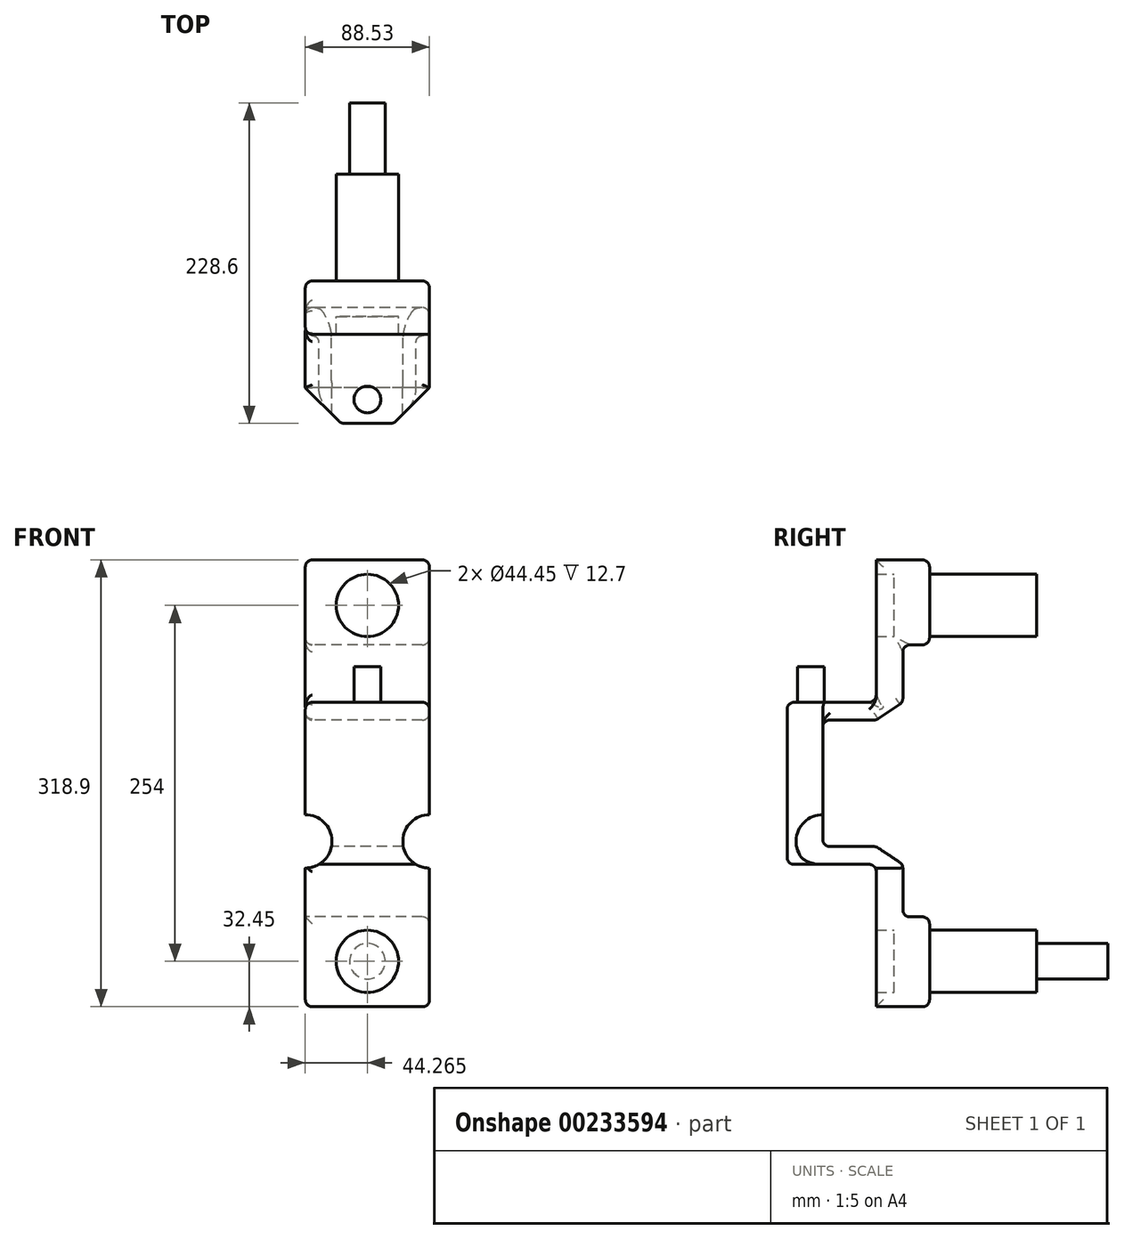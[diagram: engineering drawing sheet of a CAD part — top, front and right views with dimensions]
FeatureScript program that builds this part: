
annotation { "Feature Type Name" : "Feature", "Feature Type Description" : "" }
export const myFeature = defineFeature(function(context is Context, id is Id, definition is map)
    precondition{}
    {
        {
            var Q0;
            Q0=qCreatedBy(makeId("Front.planeOp"),FACE);
            var sketch = newSketch(context, id + "F0", { "sketchPlane" : qUnion([Q0])});
            skPoint(sketch, "E0.middle", {"position": v(-200.62, 122.45) * mm});
            skCircle(sketch, "E1", {"center": v(-200.62, 122.45) * mm, "radius": 22.23 * mm});
            skCircle(sketch, "E2", {"center": v(-200.62, -131.55) * mm, "radius": 22.23 * mm});
            skLineSegment(sketch, "E3", {"start": v(-200.62, 122.45) * mm, "end": v(-200.62, -131.55) * mm, "construction": true});
            skLineSegment(sketch, "E4.bottom", {"start": v(-156.36, -164) * mm, "end": v(-244.9, -164) * mm});
            skLineSegment(sketch, "E4.top", {"start": v(-156.36, 154.9) * mm, "end": v(-244.9, 154.9) * mm});
            skLineSegment(sketch, "E4.left", {"start": v(-156.36, -164) * mm, "end": v(-156.36, 154.9) * mm});
            skLineSegment(sketch, "E4.right", {"start": v(-244.9, -164) * mm, "end": v(-244.9, 154.9) * mm});
            skPoint(sketch, "E4.middle", {"position": v(-200.62, -4.55) * mm});
            skSolve(sketch);
        }
        {
            var Q0;
            Q0=qSketchRegion(id+"F0",true);
            extrude(context, id + "F1", {"entities" : qUnion([Q0]), "depth" : 76.2 * mm});
        }
        {
            var Q0;
            Q0=makeQuery(id+"F1.opExtrude","SWEPT_FACE",FACE,{"disambiguationData":[OSD([sQuery(id+"F0.wireOp",EDGE,"E4.right")])]});
            var sketch = newSketch(context, id + "F2", { "sketchPlane" : qUnion([Q0])});
            skLineSegment(sketch, "E5", {"start": v(76.2, 154.9) * mm, "end": v(76.2, 53.3) * mm, "construction": true});
            skLineSegment(sketch, "E6", {"start": v(76.2, -164) * mm, "end": v(50.8, -164) * mm, "construction": true});
            skLineSegment(sketch, "E7", {"start": v(76.2, -164) * mm, "end": v(76.2, -62.4) * mm, "construction": true});
            skLineSegment(sketch, "E8", {"start": v(76.2, 154.9) * mm, "end": v(50.8, 154.9) * mm, "construction": true});
            skLineSegment(sketch, "E9", {"start": v(38.1, 154.9) * mm, "end": v(76.2, 53.3) * mm});
            skLineSegment(sketch, "E10", {"start": v(76.2, -62.4) * mm, "end": v(38.1, -164) * mm});
            skSolve(sketch);
        }
        {
            var Q0;
            {var subQ0=sQuery(id+"F2.wireOp",EDGE,"E10");Q0=makeQuery(id+"F2.imprint","IMPRINT",FACE,{"disambiguationData":[TD([[makeQuery(id+"F2.imprint","IMPRINT",EDGE,{"derivedFrom":subQ0}),1.0]])]});}
            var Q1;
            {var subQ0=sQuery(id+"F2.wireOp",EDGE,"E9");Q1=makeQuery(id+"F2.imprint","IMPRINT",FACE,{"disambiguationData":[TD([[makeQuery(id+"F2.imprint","IMPRINT",EDGE,{"derivedFrom":subQ0}),1.0]])]});}
            extrude(context, id + "F3", {"entities" : qUnion([Q0, Q1]), "operationType" : NewBodyOperationType.REMOVE, "endBound" : BoundingType.THROUGH_ALL, "oppositeDirection" : true, "depth" : 25.4 * mm});
        }
        {
            var Q0;
            Q0=makeQuery(id+"F0.imprint","IMPRINT",FACE,{"disambiguationData":[TD([[makeQuery(id+"F0.imprint","IMPRINT",EDGE,{"derivedFrom":sQuery(id+"F0.wireOp",EDGE,"E1")}),1.0]])]});
            var Q1;
            Q1=makeQuery(id+"F0.imprint","IMPRINT",FACE,{"disambiguationData":[TD([[makeQuery(id+"F0.imprint","IMPRINT",EDGE,{"derivedFrom":sQuery(id+"F0.wireOp",EDGE,"E2")}),1.0]])]});
            extrude(context, id + "F4", {"entities" : qUnion([Q0, Q1]), "operationType" : NewBodyOperationType.ADD, "depth" : 25.4 * mm, "hasSecondDirection" : true, "secondDirectionOppositeDirection" : true, "secondDirectionDepth" : 76.2 * mm});
        }
        {
            var Q0;
            Q0=makeQuery(id+"F1.opExtrude","SWEPT_FACE",FACE,{"disambiguationData":[OSD([sQuery(id+"F0.wireOp",EDGE,"E4.left")])]});
            var sketch = newSketch(context, id + "F5", { "sketchPlane" : qUnion([Q0])});
            skLineSegment(sketch, "E11", {"start": v(-38.1, 154.9) * mm, "end": v(-38.1, 53.3) * mm});
            skLineSegment(sketch, "E12", {"start": v(-38.1, 53.3) * mm, "end": v(-76.2, 53.3) * mm});
            skLineSegment(sketch, "E13", {"start": v(-76.2, -62.4) * mm, "end": v(-38.1, -62.4) * mm});
            skLineSegment(sketch, "E14", {"start": v(-38.1, -62.4) * mm, "end": v(-38.1, -164) * mm});
            skSolve(sketch);
        }
        {
            var Q0;
            Q0=makeQuery(id+"F5.imprint","IMPRINT",FACE,{"disambiguationData":[TD([[makeQuery(id+"F5.imprint","IMPRINT",EDGE,{"derivedFrom":sQuery(id+"F5.wireOp",EDGE,"E13")}),-1.0]])]});
            var Q1;
            Q1=makeQuery(id+"F5.imprint","IMPRINT",FACE,{"disambiguationData":[TD([[makeQuery(id+"F5.imprint","IMPRINT",EDGE,{"derivedFrom":sQuery(id+"F5.wireOp",EDGE,"E11")}),-1.0]])]});
            extrude(context, id + "F6", {"entities" : qUnion([Q0, Q1]), "operationType" : NewBodyOperationType.REMOVE, "endBound" : BoundingType.THROUGH_ALL, "oppositeDirection" : true, "depth" : 25.4 * mm});
        }
        {
            var Q0;
            Q0=makeQuery(id+"F4.opExtrude","CAP_FACE",FACE,{"disambiguationData":[OSD([sQuery(id+"F0.wireOp",EDGE,"E2")])],"isStart":true});
            extrude(context, id + "F7", {"entities" : qUnion([Q0]), "operationType" : NewBodyOperationType.ADD, "depth" : 50.8 * mm});
        }
        {
            var Q0;
            Q0=makeQuery(id+"F7.opExtrude","CAP_FACE",FACE,{"disambiguationData":[OSD([sQuery(id+"F0.wireOp",EDGE,"E2")])],"isStart":false});
            var sketch = newSketch(context, id + "F8", { "sketchPlane" : qUnion([Q0])});
            skCircle(sketch, "E15", {"center": v(200.62, -131.55) * mm, "radius": 12.7 * mm});
            skSolve(sketch);
        }
        {
            var Q0;
            Q0=makeQuery(id+"F8.imprint","IMPRINT",FACE,{"disambiguationData":[TD([[makeQuery(id+"F8.imprint","IMPRINT",EDGE,{"derivedFrom":sQuery(id+"F8.wireOp",EDGE,"E15")}),-1.0]])]});
            extrude(context, id + "F9", {"entities" : qUnion([Q0]), "operationType" : NewBodyOperationType.REMOVE, "oppositeDirection" : true, "depth" : 50.8 * mm});
        }
        {
            var Q0;
            Q0=makeQuery(id+"F1.opExtrude","CAP_FACE",FACE,{"disambiguationData":[OSD([sQuery(id+"F0.wireOp",EDGE,"E1"),sQuery(id+"F0.wireOp",EDGE,"E2"),sQuery(id+"F0.wireOp",EDGE,"E4.bottom"),sQuery(id+"F0.wireOp",EDGE,"E4.top"),sQuery(id+"F0.wireOp",EDGE,"E4.left"),sQuery(id+"F0.wireOp",EDGE,"E4.right")])],"isStart":false});
            extrude(context, id + "F10", {"entities" : qUnion([Q0]), "operationType" : NewBodyOperationType.ADD, "depth" : 25.4 * mm});
        }
        {
            var Q0;
            {var subQ0=sQuery(id+"F5.wireOp",EDGE,"E12");Q0=makeQuery(id+"F10.boolean.opBoolean","MERGE",FACE,{"derivedFrom":[makeQuery(id+"F6.boolean.opBoolean","COPY",FACE,{"derivedFrom":makeQuery(id+"F6.opExtrude","SWEPT_FACE",FACE,{"disambiguationData":[OSD([subQ0])]})}),makeQuery(id+"F10.opExtrude","SWEPT_FACE",FACE,{"disambiguationData":[OSD([sQuery(id+"F0.wireOp",EDGE,"E4.left"),sQuery(id+"F0.wireOp",EDGE,"E4.right"),sQuery(id+"F2.wireOp",EDGE,"E9"),subQ0])]})]});}
            var sketch = newSketch(context, id + "F11", { "sketchPlane" : qUnion([Q0])});
            skCircle(sketch, "E16", {"center": v(-200.62, -84.67) * mm, "radius": 9.53 * mm});
            skPoint(sketch, "E16.centerSnap0", {"position": v(-200.62, -101.6) * mm});
            skSolve(sketch);
        }
        {
            var Q0;
            Q0=makeQuery(id+"F11.imprint","IMPRINT",FACE,{"disambiguationData":[TD([[makeQuery(id+"F11.imprint","IMPRINT",EDGE,{"derivedFrom":sQuery(id+"F11.wireOp",EDGE,"E16")}),1.0]])]});
            extrude(context, id + "F12", {"entities" : qUnion([Q0]), "operationType" : NewBodyOperationType.ADD, "depth" : 25.4 * mm});
        }
        {
            var Q0;
            Q0=makeQuery(id+"F10.opExtrude","CAP_EDGE",EDGE,{"disambiguationData":[OSD([sQuery(id+"F0.wireOp",EDGE,"E4.right")])],"isStart":false});
            var Q1;
            Q1=makeQuery(id+"F10.opExtrude","CAP_EDGE",EDGE,{"disambiguationData":[OSD([sQuery(id+"F0.wireOp",EDGE,"E4.left")])],"isStart":false});
            chamfer(context, id + "F13", {"entities" : qUnion([Q0, Q1]), "width" : 25.4 * mm, "tangentPropagation" : true});
        }
        {
            var Q0;
            {var subQ0=sQuery(id+"F0.wireOp",EDGE,"E4.right");Q0=makeQuery(id+"F10.boolean.opBoolean","MERGE",FACE,{"derivedFrom":[makeQuery(id+"F1.opExtrude","SWEPT_FACE",FACE,{"disambiguationData":[OSD([subQ0])]}),makeQuery(id+"F10.opExtrude","SWEPT_FACE",FACE,{"disambiguationData":[OSD([subQ0])]})]});}
            var sketch = newSketch(context, id + "F14", { "sketchPlane" : qUnion([Q0])});
            skLineSegment(sketch, "E17", {"start": v(0, 94.28) * mm, "end": v(19.05, 94.28) * mm});
            skLineSegment(sketch, "E18", {"start": v(19.05, 94.28) * mm, "end": v(19.05, 53.3) * mm});
            skLineSegment(sketch, "E19", {"start": v(19.05, -99.86) * mm, "end": v(0, -99.86) * mm});
            skLineSegment(sketch, "E20.0", {"start": v(76.2, 40.6) * mm, "end": v(38.1, 40.6) * mm});
            skLineSegment(sketch, "E21.0", {"start": v(38.1, -49.7) * mm, "end": v(76.2, -49.7) * mm});
            skLineSegment(sketch, "E22", {"start": v(38.1, 40.6) * mm, "end": v(19.05, 53.3) * mm});
            skLineSegment(sketch, "E23", {"start": v(38.1, -49.7) * mm, "end": v(19.05, -62.4) * mm});
            skLineSegment(sketch, "E24.trimOffspring", {"start": v(19.05, -62.4) * mm, "end": v(19.05, -99.86) * mm});
            skSolve(sketch);
        }
        {
            var Q0;
            {var subQ2=sQuery(id+"F14.wireOp",EDGE,"E17");Q0=makeQuery(id+"F14.imprint","IMPRINT",FACE,{"disambiguationData":[TD([[makeQuery(id+"F14.imprint","IMPRINT",EDGE,{"derivedFrom":subQ2}),-1.0]])]});}
            extrude(context, id + "F15", {"entities" : qUnion([Q0]), "operationType" : NewBodyOperationType.REMOVE, "endBound" : BoundingType.THROUGH_ALL, "oppositeDirection" : true, "depth" : 25.4 * mm});
        }
        {
            var Q0;
            {var subQ0=sQuery(id+"F5.wireOp",EDGE,"E13");var subQ1=sQuery(id+"F0.wireOp",EDGE,"E4.left");Q0=makeQuery(id+"F13.opChamfer","BLEND_EDGE",EDGE,{"blendedFrom":[makeQuery(id+"F10.opExtrude","CAP_EDGE",EDGE,{"disambiguationData":[OSD([subQ1])],"isStart":false}),makeQuery(id+"F10.boolean.opBoolean","MERGE",FACE,{"derivedFrom":[makeQuery(id+"F6.boolean.opBoolean","COPY",FACE,{"derivedFrom":makeQuery(id+"F6.opExtrude","SWEPT_FACE",FACE,{"disambiguationData":[OSD([subQ0])]})}),makeQuery(id+"F10.opExtrude","SWEPT_FACE",FACE,{"disambiguationData":[OSD([subQ1,sQuery(id+"F0.wireOp",EDGE,"E4.right"),sQuery(id+"F2.wireOp",EDGE,"E10"),subQ0])]})]})],"blendedInto":[makeQuery(id+"F10.boolean.opBoolean","MERGE",FACE,{"derivedFrom":[makeQuery(id+"F6.boolean.opBoolean","COPY",FACE,{"derivedFrom":makeQuery(id+"F6.opExtrude","SWEPT_FACE",FACE,{"disambiguationData":[OSD([subQ0])]})}),makeQuery(id+"F10.opExtrude","SWEPT_FACE",FACE,{"disambiguationData":[OSD([subQ1,sQuery(id+"F0.wireOp",EDGE,"E4.right"),sQuery(id+"F2.wireOp",EDGE,"E10"),subQ0])]})]})]});}
            var Q1;
            Q1=makeQuery(id+"F10.opExtrude","CAP_EDGE",EDGE,{"disambiguationData":[OSD([sQuery(id+"F0.wireOp",EDGE,"E4.left"),sQuery(id+"F0.wireOp",EDGE,"E4.right"),sQuery(id+"F2.wireOp",EDGE,"E10"),sQuery(id+"F5.wireOp",EDGE,"E13")])],"isStart":false});
            var Q2;
            {var subQ0=sQuery(id+"F5.wireOp",EDGE,"E13");var subQ1=sQuery(id+"F0.wireOp",EDGE,"E4.right");Q2=makeQuery(id+"F13.opChamfer","BLEND_EDGE",EDGE,{"blendedFrom":[makeQuery(id+"F10.opExtrude","CAP_EDGE",EDGE,{"disambiguationData":[OSD([subQ1])],"isStart":false}),makeQuery(id+"F10.boolean.opBoolean","MERGE",FACE,{"derivedFrom":[makeQuery(id+"F6.boolean.opBoolean","COPY",FACE,{"derivedFrom":makeQuery(id+"F6.opExtrude","SWEPT_FACE",FACE,{"disambiguationData":[OSD([subQ0])]})}),makeQuery(id+"F10.opExtrude","SWEPT_FACE",FACE,{"disambiguationData":[OSD([sQuery(id+"F0.wireOp",EDGE,"E4.left"),subQ1,sQuery(id+"F2.wireOp",EDGE,"E10"),subQ0])]})]})],"blendedInto":[makeQuery(id+"F10.boolean.opBoolean","MERGE",FACE,{"derivedFrom":[makeQuery(id+"F6.boolean.opBoolean","COPY",FACE,{"derivedFrom":makeQuery(id+"F6.opExtrude","SWEPT_FACE",FACE,{"disambiguationData":[OSD([subQ0])]})}),makeQuery(id+"F10.opExtrude","SWEPT_FACE",FACE,{"disambiguationData":[OSD([sQuery(id+"F0.wireOp",EDGE,"E4.left"),subQ1,sQuery(id+"F2.wireOp",EDGE,"E10"),subQ0])]})]})]});}
            var Q3;
            {var subQ0=sQuery(id+"F0.wireOp",EDGE,"E4.right");Q3=makeQuery(id+"F10.boolean.opBoolean","MERGE",EDGE,{"derivedFrom":[makeQuery(id+"F6.boolean.opBoolean","INTERSECT",EDGE,{"derivedFrom":[makeQuery(id+"F1.opExtrude","SWEPT_FACE",FACE,{"disambiguationData":[OSD([subQ0])]}),makeQuery(id+"F6.opExtrude","SWEPT_FACE",FACE,{"disambiguationData":[OSD([sQuery(id+"F5.wireOp",EDGE,"E13")])]})]}),makeQuery(id+"F10.opExtrude","SWEPT_EDGE",EDGE,{"disambiguationData":[OSD([subQ0,sQuery(id+"F2.wireOp",EDGE,"E10")])]})]});}
            var Q4;
            Q4=makeQuery(id+"F6.boolean.opBoolean","INTERSECT",EDGE,{"derivedFrom":[makeQuery(id+"F1.opExtrude","SWEPT_FACE",FACE,{"disambiguationData":[OSD([sQuery(id+"F0.wireOp",EDGE,"E4.right")])]}),makeQuery(id+"F6.opExtrude","SWEPT_FACE",FACE,{"disambiguationData":[OSD([sQuery(id+"F5.wireOp",EDGE,"E14")])]})]});
            var Q5;
            {var subQ0=sQuery(id+"F2.wireOp",EDGE,"E10");var subQ1=sQuery(id+"F0.wireOp",EDGE,"E4.bottom");Q5=makeQuery(id+"F6.boolean.opBoolean","MERGE",EDGE,{"derivedFrom":[makeQuery(id+"F3.boolean.opBoolean","COPY",EDGE,{"derivedFrom":makeQuery(id+"F3.opExtrude","SWEPT_EDGE",EDGE,{"disambiguationData":[OSD([subQ1,sQuery(id+"F0.wireOp",EDGE,"E4.right"),subQ0])]})}),makeQuery(id+"F6.opExtrude","SWEPT_EDGE",EDGE,{"disambiguationData":[OSD([subQ1,sQuery(id+"F0.wireOp",EDGE,"E4.left"),subQ0,sQuery(id+"F5.wireOp",EDGE,"E14")])]})]});}
            var Q6;
            Q6=makeQuery(id+"F6.boolean.opBoolean","COPY",EDGE,{"derivedFrom":makeQuery(id+"F6.opExtrude","CAP_EDGE",EDGE,{"disambiguationData":[OSD([sQuery(id+"F5.wireOp",EDGE,"E14")])],"isStart":true})});
            var Q7;
            {var subQ0=sQuery(id+"F5.wireOp",EDGE,"E13");Q7=makeQuery(id+"F10.boolean.opBoolean","MERGE",EDGE,{"derivedFrom":[makeQuery(id+"F6.boolean.opBoolean","COPY",EDGE,{"derivedFrom":makeQuery(id+"F6.opExtrude","CAP_EDGE",EDGE,{"disambiguationData":[OSD([subQ0])],"isStart":true})}),makeQuery(id+"F10.opExtrude","SWEPT_EDGE",EDGE,{"disambiguationData":[OSD([sQuery(id+"F0.wireOp",EDGE,"E4.left"),sQuery(id+"F2.wireOp",EDGE,"E10"),subQ0])]})]});}
            var Q8;
            {var subQ0=sQuery(id+"F0.wireOp",EDGE,"E4.left");Q8=makeQuery(id+"F13.opChamfer","BLEND_EDGE",EDGE,{"blendedFrom":[makeQuery(id+"F10.opExtrude","CAP_EDGE",EDGE,{"disambiguationData":[OSD([subQ0])],"isStart":false}),makeQuery(id+"F10.opExtrude","CAP_FACE",FACE,{"disambiguationData":[OSD([sQuery(id+"F0.wireOp",EDGE,"E1"),sQuery(id+"F0.wireOp",EDGE,"E2"),sQuery(id+"F0.wireOp",EDGE,"E4.bottom"),sQuery(id+"F0.wireOp",EDGE,"E4.top"),subQ0,sQuery(id+"F0.wireOp",EDGE,"E4.right")])],"isStart":false})],"blendedInto":[makeQuery(id+"F10.opExtrude","CAP_FACE",FACE,{"disambiguationData":[OSD([sQuery(id+"F0.wireOp",EDGE,"E1"),sQuery(id+"F0.wireOp",EDGE,"E2"),sQuery(id+"F0.wireOp",EDGE,"E4.bottom"),sQuery(id+"F0.wireOp",EDGE,"E4.top"),subQ0,sQuery(id+"F0.wireOp",EDGE,"E4.right")])],"isStart":false})]});}
            var Q9;
            {var subQ0=sQuery(id+"F0.wireOp",EDGE,"E4.right");Q9=makeQuery(id+"F13.opChamfer","BLEND_EDGE",EDGE,{"blendedFrom":[makeQuery(id+"F10.opExtrude","CAP_EDGE",EDGE,{"disambiguationData":[OSD([subQ0])],"isStart":false}),makeQuery(id+"F10.opExtrude","CAP_FACE",FACE,{"disambiguationData":[OSD([sQuery(id+"F0.wireOp",EDGE,"E1"),sQuery(id+"F0.wireOp",EDGE,"E2"),sQuery(id+"F0.wireOp",EDGE,"E4.bottom"),sQuery(id+"F0.wireOp",EDGE,"E4.top"),sQuery(id+"F0.wireOp",EDGE,"E4.left"),subQ0])],"isStart":false})],"blendedInto":[makeQuery(id+"F10.opExtrude","CAP_FACE",FACE,{"disambiguationData":[OSD([sQuery(id+"F0.wireOp",EDGE,"E1"),sQuery(id+"F0.wireOp",EDGE,"E2"),sQuery(id+"F0.wireOp",EDGE,"E4.bottom"),sQuery(id+"F0.wireOp",EDGE,"E4.top"),sQuery(id+"F0.wireOp",EDGE,"E4.left"),subQ0])],"isStart":false})]});}
            var Q10;
            {var subQ0=sQuery(id+"F5.wireOp",EDGE,"E12");var subQ1=sQuery(id+"F0.wireOp",EDGE,"E4.left");Q10=makeQuery(id+"F13.opChamfer","BLEND_EDGE",EDGE,{"blendedFrom":[makeQuery(id+"F10.opExtrude","CAP_EDGE",EDGE,{"disambiguationData":[OSD([subQ1])],"isStart":false}),makeQuery(id+"F10.boolean.opBoolean","MERGE",FACE,{"derivedFrom":[makeQuery(id+"F6.boolean.opBoolean","COPY",FACE,{"derivedFrom":makeQuery(id+"F6.opExtrude","SWEPT_FACE",FACE,{"disambiguationData":[OSD([subQ0])]})}),makeQuery(id+"F10.opExtrude","SWEPT_FACE",FACE,{"disambiguationData":[OSD([subQ1,sQuery(id+"F0.wireOp",EDGE,"E4.right"),sQuery(id+"F2.wireOp",EDGE,"E9"),subQ0])]})]})],"blendedInto":[makeQuery(id+"F10.boolean.opBoolean","MERGE",FACE,{"derivedFrom":[makeQuery(id+"F6.boolean.opBoolean","COPY",FACE,{"derivedFrom":makeQuery(id+"F6.opExtrude","SWEPT_FACE",FACE,{"disambiguationData":[OSD([subQ0])]})}),makeQuery(id+"F10.opExtrude","SWEPT_FACE",FACE,{"disambiguationData":[OSD([subQ1,sQuery(id+"F0.wireOp",EDGE,"E4.right"),sQuery(id+"F2.wireOp",EDGE,"E9"),subQ0])]})]})]});}
            var Q11;
            Q11=makeQuery(id+"F10.opExtrude","CAP_EDGE",EDGE,{"disambiguationData":[OSD([sQuery(id+"F0.wireOp",EDGE,"E4.left"),sQuery(id+"F0.wireOp",EDGE,"E4.right"),sQuery(id+"F2.wireOp",EDGE,"E9"),sQuery(id+"F5.wireOp",EDGE,"E12")])],"isStart":false});
            var Q12;
            {var subQ0=sQuery(id+"F5.wireOp",EDGE,"E12");var subQ1=sQuery(id+"F0.wireOp",EDGE,"E4.right");Q12=makeQuery(id+"F13.opChamfer","BLEND_EDGE",EDGE,{"blendedFrom":[makeQuery(id+"F10.opExtrude","CAP_EDGE",EDGE,{"disambiguationData":[OSD([subQ1])],"isStart":false}),makeQuery(id+"F10.boolean.opBoolean","MERGE",FACE,{"derivedFrom":[makeQuery(id+"F6.boolean.opBoolean","COPY",FACE,{"derivedFrom":makeQuery(id+"F6.opExtrude","SWEPT_FACE",FACE,{"disambiguationData":[OSD([subQ0])]})}),makeQuery(id+"F10.opExtrude","SWEPT_FACE",FACE,{"disambiguationData":[OSD([sQuery(id+"F0.wireOp",EDGE,"E4.left"),subQ1,sQuery(id+"F2.wireOp",EDGE,"E9"),subQ0])]})]})],"blendedInto":[makeQuery(id+"F10.boolean.opBoolean","MERGE",FACE,{"derivedFrom":[makeQuery(id+"F6.boolean.opBoolean","COPY",FACE,{"derivedFrom":makeQuery(id+"F6.opExtrude","SWEPT_FACE",FACE,{"disambiguationData":[OSD([subQ0])]})}),makeQuery(id+"F10.opExtrude","SWEPT_FACE",FACE,{"disambiguationData":[OSD([sQuery(id+"F0.wireOp",EDGE,"E4.left"),subQ1,sQuery(id+"F2.wireOp",EDGE,"E9"),subQ0])]})]})]});}
            var Q13;
            Q13=makeQuery(id+"F6.boolean.opBoolean","INTERSECT",EDGE,{"derivedFrom":[makeQuery(id+"F1.opExtrude","SWEPT_FACE",FACE,{"disambiguationData":[OSD([sQuery(id+"F0.wireOp",EDGE,"E4.right")])]}),makeQuery(id+"F6.opExtrude","SWEPT_FACE",FACE,{"disambiguationData":[OSD([sQuery(id+"F5.wireOp",EDGE,"E11")])]})]});
            var Q14;
            {var subQ0=sQuery(id+"F2.wireOp",EDGE,"E9");var subQ1=sQuery(id+"F0.wireOp",EDGE,"E4.top");Q14=makeQuery(id+"F6.boolean.opBoolean","MERGE",EDGE,{"derivedFrom":[makeQuery(id+"F3.boolean.opBoolean","COPY",EDGE,{"derivedFrom":makeQuery(id+"F3.opExtrude","SWEPT_EDGE",EDGE,{"disambiguationData":[OSD([subQ1,sQuery(id+"F0.wireOp",EDGE,"E4.right"),subQ0])]})}),makeQuery(id+"F6.opExtrude","SWEPT_EDGE",EDGE,{"disambiguationData":[OSD([subQ1,sQuery(id+"F0.wireOp",EDGE,"E4.left"),subQ0,sQuery(id+"F5.wireOp",EDGE,"E11")])]})]});}
            var Q15;
            Q15=makeQuery(id+"F6.boolean.opBoolean","COPY",EDGE,{"derivedFrom":makeQuery(id+"F6.opExtrude","CAP_EDGE",EDGE,{"disambiguationData":[OSD([sQuery(id+"F5.wireOp",EDGE,"E11")])],"isStart":true})});
            var Q16;
            Q16=makeQuery(id+"F1.opExtrude","SWEPT_EDGE",EDGE,{"disambiguationData":[OSD([sQuery(id+"F0.wireOp",EDGE,"E4.top"),sQuery(id+"F0.wireOp",EDGE,"E4.left")])]});
            var Q17;
            {var subQ0=sQuery(id+"F0.wireOp",EDGE,"E4.left");var subQ1=sQuery(id+"F0.wireOp",EDGE,"E4.top");Q17=makeQuery(id+"F15.boolean.opBoolean","SPLIT",EDGE,{"disambiguationData":[TD([makeQuery(id+"F1.opExtrude","SWEPT_FACE",FACE,{"disambiguationData":[OSD([subQ1])]})])],"derivedFrom":makeQuery(id+"F1.opExtrude","CAP_EDGE",EDGE,{"disambiguationData":[OSD([subQ0])],"isStart":true})});}
            var Q18;
            {var subQ0=sQuery(id+"F0.wireOp",EDGE,"E4.left");Q18=makeQuery(id+"F15.boolean.opBoolean","INTERSECT",EDGE,{"derivedFrom":[makeQuery(id+"F10.boolean.opBoolean","MERGE",FACE,{"derivedFrom":[makeQuery(id+"F1.opExtrude","SWEPT_FACE",FACE,{"disambiguationData":[OSD([subQ0])]}),makeQuery(id+"F10.opExtrude","SWEPT_FACE",FACE,{"disambiguationData":[OSD([subQ0])]})]}),makeQuery(id+"F15.opExtrude","SWEPT_FACE",FACE,{"disambiguationData":[OSD([sQuery(id+"F14.wireOp",EDGE,"E21.0")])]})]});}
            var Q19;
            {var subQ0=sQuery(id+"F0.wireOp",EDGE,"E4.left");Q19=makeQuery(id+"F15.boolean.opBoolean","INTERSECT",EDGE,{"derivedFrom":[makeQuery(id+"F10.boolean.opBoolean","MERGE",FACE,{"derivedFrom":[makeQuery(id+"F1.opExtrude","SWEPT_FACE",FACE,{"disambiguationData":[OSD([subQ0])]}),makeQuery(id+"F10.opExtrude","SWEPT_FACE",FACE,{"disambiguationData":[OSD([subQ0])]})]}),makeQuery(id+"F15.opExtrude","SWEPT_FACE",FACE,{"disambiguationData":[OSD([sQuery(id+"F14.wireOp",EDGE,"E23")])]})]});}
            var Q20;
            {var subQ0=sQuery(id+"F0.wireOp",EDGE,"E4.left");Q20=makeQuery(id+"F15.boolean.opBoolean","INTERSECT",EDGE,{"derivedFrom":[makeQuery(id+"F10.boolean.opBoolean","MERGE",FACE,{"derivedFrom":[makeQuery(id+"F1.opExtrude","SWEPT_FACE",FACE,{"disambiguationData":[OSD([subQ0])]}),makeQuery(id+"F10.opExtrude","SWEPT_FACE",FACE,{"disambiguationData":[OSD([subQ0])]})]}),makeQuery(id+"F15.opExtrude","SWEPT_FACE",FACE,{"disambiguationData":[OSD([sQuery(id+"F14.wireOp",EDGE,"E24.trimOffspring")])]})]});}
            var Q21;
            {var subQ0=sQuery(id+"F0.wireOp",EDGE,"E4.left");Q21=makeQuery(id+"F15.boolean.opBoolean","INTERSECT",EDGE,{"derivedFrom":[makeQuery(id+"F10.boolean.opBoolean","MERGE",FACE,{"derivedFrom":[makeQuery(id+"F1.opExtrude","SWEPT_FACE",FACE,{"disambiguationData":[OSD([subQ0])]}),makeQuery(id+"F10.opExtrude","SWEPT_FACE",FACE,{"disambiguationData":[OSD([subQ0])]})]}),makeQuery(id+"F15.opExtrude","SWEPT_FACE",FACE,{"disambiguationData":[OSD([sQuery(id+"F14.wireOp",EDGE,"E19")])]})]});}
            var Q22;
            {var subQ0=sQuery(id+"F0.wireOp",EDGE,"E4.left");var subQ1=sQuery(id+"F0.wireOp",EDGE,"E4.bottom");Q22=makeQuery(id+"F15.boolean.opBoolean","SPLIT",EDGE,{"disambiguationData":[TD([makeQuery(id+"F1.opExtrude","SWEPT_FACE",FACE,{"disambiguationData":[OSD([subQ1])]})])],"derivedFrom":makeQuery(id+"F1.opExtrude","CAP_EDGE",EDGE,{"disambiguationData":[OSD([subQ0])],"isStart":true})});}
            var Q23;
            Q23=makeQuery(id+"F1.opExtrude","SWEPT_EDGE",EDGE,{"disambiguationData":[OSD([sQuery(id+"F0.wireOp",EDGE,"E4.bottom"),sQuery(id+"F0.wireOp",EDGE,"E4.left")])]});
            var Q24;
            Q24=makeQuery(id+"F1.opExtrude","CAP_EDGE",EDGE,{"disambiguationData":[OSD([sQuery(id+"F0.wireOp",EDGE,"E4.bottom")])],"isStart":true});
            var Q25;
            Q25=makeQuery(id+"F1.opExtrude","SWEPT_EDGE",EDGE,{"disambiguationData":[OSD([sQuery(id+"F0.wireOp",EDGE,"E4.bottom"),sQuery(id+"F0.wireOp",EDGE,"E4.right")])]});
            var Q26;
            {var subQ0=sQuery(id+"F0.wireOp",EDGE,"E4.right");var subQ1=sQuery(id+"F0.wireOp",EDGE,"E4.bottom");Q26=makeQuery(id+"F15.boolean.opBoolean","SPLIT",EDGE,{"disambiguationData":[TD([makeQuery(id+"F1.opExtrude","SWEPT_FACE",FACE,{"disambiguationData":[OSD([subQ1])]})])],"derivedFrom":makeQuery(id+"F1.opExtrude","CAP_EDGE",EDGE,{"disambiguationData":[OSD([subQ0])],"isStart":true})});}
            var Q27;
            Q27=makeQuery(id+"F15.boolean.opBoolean","COPY",EDGE,{"derivedFrom":makeQuery(id+"F15.opExtrude","CAP_EDGE",EDGE,{"disambiguationData":[OSD([sQuery(id+"F14.wireOp",EDGE,"E19")])],"isStart":true})});
            var Q28;
            Q28=makeQuery(id+"F15.boolean.opBoolean","COPY",EDGE,{"derivedFrom":makeQuery(id+"F15.opExtrude","CAP_EDGE",EDGE,{"disambiguationData":[OSD([sQuery(id+"F14.wireOp",EDGE,"E24.trimOffspring")])],"isStart":true})});
            var Q29;
            Q29=makeQuery(id+"F15.boolean.opBoolean","COPY",EDGE,{"derivedFrom":makeQuery(id+"F15.opExtrude","CAP_EDGE",EDGE,{"disambiguationData":[OSD([sQuery(id+"F14.wireOp",EDGE,"E23")])],"isStart":true})});
            var Q30;
            Q30=makeQuery(id+"F15.boolean.opBoolean","COPY",EDGE,{"derivedFrom":makeQuery(id+"F15.opExtrude","CAP_EDGE",EDGE,{"disambiguationData":[OSD([sQuery(id+"F14.wireOp",EDGE,"E21.0")])],"isStart":true})});
            var Q31;
            Q31=makeQuery(id+"F15.boolean.opBoolean","COPY",EDGE,{"derivedFrom":makeQuery(id+"F15.opExtrude","CAP_EDGE",EDGE,{"disambiguationData":[OSD([sQuery(id+"F14.wireOp",EDGE,"E20.0")])],"isStart":true})});
            var Q32;
            Q32=makeQuery(id+"F15.boolean.opBoolean","COPY",EDGE,{"derivedFrom":makeQuery(id+"F15.opExtrude","CAP_EDGE",EDGE,{"disambiguationData":[OSD([sQuery(id+"F14.wireOp",EDGE,"E22")])],"isStart":true})});
            var Q33;
            Q33=makeQuery(id+"F15.boolean.opBoolean","COPY",EDGE,{"derivedFrom":makeQuery(id+"F15.opExtrude","CAP_EDGE",EDGE,{"disambiguationData":[OSD([sQuery(id+"F14.wireOp",EDGE,"E18")])],"isStart":true})});
            var Q34;
            Q34=makeQuery(id+"F15.boolean.opBoolean","COPY",EDGE,{"derivedFrom":makeQuery(id+"F15.opExtrude","CAP_EDGE",EDGE,{"disambiguationData":[OSD([sQuery(id+"F14.wireOp",EDGE,"E17")])],"isStart":true})});
            var Q35;
            {var subQ0=sQuery(id+"F0.wireOp",EDGE,"E4.right");var subQ1=sQuery(id+"F0.wireOp",EDGE,"E4.top");Q35=makeQuery(id+"F15.boolean.opBoolean","SPLIT",EDGE,{"disambiguationData":[TD([makeQuery(id+"F1.opExtrude","SWEPT_FACE",FACE,{"disambiguationData":[OSD([subQ1])]})])],"derivedFrom":makeQuery(id+"F1.opExtrude","CAP_EDGE",EDGE,{"disambiguationData":[OSD([subQ0])],"isStart":true})});}
            var Q36;
            Q36=makeQuery(id+"F1.opExtrude","SWEPT_EDGE",EDGE,{"disambiguationData":[OSD([sQuery(id+"F0.wireOp",EDGE,"E4.top"),sQuery(id+"F0.wireOp",EDGE,"E4.right")])]});
            var Q37;
            Q37=makeQuery(id+"F1.opExtrude","CAP_EDGE",EDGE,{"disambiguationData":[OSD([sQuery(id+"F0.wireOp",EDGE,"E4.top")])],"isStart":true});
            var Q38;
            {var subQ0=sQuery(id+"F5.wireOp",EDGE,"E12");Q38=makeQuery(id+"F10.boolean.opBoolean","MERGE",EDGE,{"derivedFrom":[makeQuery(id+"F6.boolean.opBoolean","COPY",EDGE,{"derivedFrom":makeQuery(id+"F6.opExtrude","CAP_EDGE",EDGE,{"disambiguationData":[OSD([subQ0])],"isStart":true})}),makeQuery(id+"F10.opExtrude","SWEPT_EDGE",EDGE,{"disambiguationData":[OSD([sQuery(id+"F0.wireOp",EDGE,"E4.left"),sQuery(id+"F2.wireOp",EDGE,"E9"),subQ0])]})]});}
            var Q39;
            {var subQ0=sQuery(id+"F0.wireOp",EDGE,"E4.right");Q39=makeQuery(id+"F10.boolean.opBoolean","MERGE",EDGE,{"derivedFrom":[makeQuery(id+"F6.boolean.opBoolean","INTERSECT",EDGE,{"derivedFrom":[makeQuery(id+"F1.opExtrude","SWEPT_FACE",FACE,{"disambiguationData":[OSD([subQ0])]}),makeQuery(id+"F6.opExtrude","SWEPT_FACE",FACE,{"disambiguationData":[OSD([sQuery(id+"F5.wireOp",EDGE,"E12")])]})]}),makeQuery(id+"F10.opExtrude","SWEPT_EDGE",EDGE,{"disambiguationData":[OSD([subQ0,sQuery(id+"F2.wireOp",EDGE,"E9")])]})]});}
            var Q40;
            Q40=makeQuery(id+"F15.boolean.opBoolean","COPY",EDGE,{"derivedFrom":makeQuery(id+"F15.opExtrude","SWEPT_EDGE",EDGE,{"disambiguationData":[OSD([sQuery(id+"F0.wireOp",EDGE,"E4.right"),sQuery(id+"F14.wireOp",EDGE,"E19")])]})});
            var Q41;
            Q41=makeQuery(id+"F15.boolean.opBoolean","COPY",EDGE,{"derivedFrom":makeQuery(id+"F15.opExtrude","SWEPT_EDGE",EDGE,{"disambiguationData":[OSD([sQuery(id+"F14.wireOp",EDGE,"E19"),sQuery(id+"F14.wireOp",EDGE,"E24.trimOffspring")])]})});
            var Q42;
            Q42=makeQuery(id+"F15.boolean.opBoolean","COPY",EDGE,{"derivedFrom":makeQuery(id+"F15.opExtrude","SWEPT_EDGE",EDGE,{"disambiguationData":[OSD([sQuery(id+"F14.wireOp",EDGE,"E23"),sQuery(id+"F14.wireOp",EDGE,"E24.trimOffspring")])]})});
            var Q43;
            Q43=makeQuery(id+"F15.boolean.opBoolean","COPY",EDGE,{"derivedFrom":makeQuery(id+"F15.opExtrude","SWEPT_EDGE",EDGE,{"disambiguationData":[OSD([sQuery(id+"F14.wireOp",EDGE,"E21.0"),sQuery(id+"F14.wireOp",EDGE,"E23")])]})});
            fillet(context, id + "F16", {"entities" : qUnion([Q0, Q1, Q2, Q3, Q4, Q5, Q6, Q7, Q8, Q9, Q10, Q11, Q12, Q13, Q14, Q15, Q16, Q17, Q18, Q19, Q20, Q21, Q22, Q23, Q24, Q25, Q26, Q27, Q28, Q29, Q30, Q31, Q32, Q33, Q34, Q35, Q36, Q37, Q38, Q39, Q40, Q41, Q42, Q43]), "radius" : 5.08 * mm, "tangentPropagation" : true, "allowEdgeOverflow" : false});
        }
        {
            var Q0;
            {var subQ0=sQuery(id+"F0.wireOp",EDGE,"E4.left");Q0=makeQuery(id+"F15.boolean.opBoolean","INTERSECT",EDGE,{"derivedFrom":[makeQuery(id+"F10.boolean.opBoolean","MERGE",FACE,{"derivedFrom":[makeQuery(id+"F1.opExtrude","SWEPT_FACE",FACE,{"disambiguationData":[OSD([subQ0])]}),makeQuery(id+"F10.opExtrude","SWEPT_FACE",FACE,{"disambiguationData":[OSD([subQ0])]})]}),makeQuery(id+"F15.opExtrude","SWEPT_FACE",FACE,{"disambiguationData":[OSD([sQuery(id+"F14.wireOp",EDGE,"E20.0")])]})]});}
            var Q1;
            Q1=makeQuery(id+"F15.boolean.opBoolean","COPY",FACE,{"derivedFrom":makeQuery(id+"F15.opExtrude","SWEPT_FACE",FACE,{"disambiguationData":[OSD([sQuery(id+"F14.wireOp",EDGE,"E22")])]})});
            var Q2;
            {var subQ0=sQuery(id+"F0.wireOp",EDGE,"E4.left");Q2=makeQuery(id+"F15.boolean.opBoolean","INTERSECT",EDGE,{"derivedFrom":[makeQuery(id+"F10.boolean.opBoolean","MERGE",FACE,{"derivedFrom":[makeQuery(id+"F1.opExtrude","SWEPT_FACE",FACE,{"disambiguationData":[OSD([subQ0])]}),makeQuery(id+"F10.opExtrude","SWEPT_FACE",FACE,{"disambiguationData":[OSD([subQ0])]})]}),makeQuery(id+"F15.opExtrude","SWEPT_FACE",FACE,{"disambiguationData":[OSD([sQuery(id+"F14.wireOp",EDGE,"E17")])]})]});}
            var Q3;
            {var subQ0=sQuery(id+"F0.wireOp",EDGE,"E4.left");Q3=makeQuery(id+"F15.boolean.opBoolean","INTERSECT",EDGE,{"derivedFrom":[makeQuery(id+"F10.boolean.opBoolean","MERGE",FACE,{"derivedFrom":[makeQuery(id+"F1.opExtrude","SWEPT_FACE",FACE,{"disambiguationData":[OSD([subQ0])]}),makeQuery(id+"F10.opExtrude","SWEPT_FACE",FACE,{"disambiguationData":[OSD([subQ0])]})]}),makeQuery(id+"F15.opExtrude","SWEPT_FACE",FACE,{"disambiguationData":[OSD([sQuery(id+"F14.wireOp",EDGE,"E18")])]})]});}
            var Q4;
            Q4=makeQuery(id+"F15.boolean.opBoolean","COPY",EDGE,{"derivedFrom":makeQuery(id+"F15.opExtrude","SWEPT_EDGE",EDGE,{"disambiguationData":[OSD([sQuery(id+"F14.wireOp",EDGE,"E17"),sQuery(id+"F14.wireOp",EDGE,"E18")])]})});
            fillet(context, id + "F17", {"entities" : qUnion([Q0, Q1, Q2, Q3, Q4]), "radius" : 5.08 * mm, "tangentPropagation" : true, "allowEdgeOverflow" : false});
        }
        {
            var Q0;
            Q0=makeQuery(id+"F6.boolean.opBoolean","COPY",EDGE,{"derivedFrom":makeQuery(id+"F6.opExtrude","SWEPT_EDGE",EDGE,{"disambiguationData":[OSD([sQuery(id+"F5.wireOp",EDGE,"E11"),sQuery(id+"F5.wireOp",EDGE,"E12")])]})});
            var Q1;
            Q1=makeQuery(id+"F6.boolean.opBoolean","COPY",EDGE,{"derivedFrom":makeQuery(id+"F6.opExtrude","SWEPT_EDGE",EDGE,{"disambiguationData":[OSD([sQuery(id+"F5.wireOp",EDGE,"E13"),sQuery(id+"F5.wireOp",EDGE,"E14")])]})});
            fillet(context, id + "F18", {"entities" : qUnion([Q0, Q1]), "radius" : 5.08 * mm, "tangentPropagation" : true, "allowEdgeOverflow" : false});
        }
        {
            var Q0;
            Q0=makeQuery(id+"F15.boolean.opBoolean","COPY",EDGE,{"derivedFrom":makeQuery(id+"F15.opExtrude","SWEPT_EDGE",EDGE,{"disambiguationData":[OSD([sQuery(id+"F0.wireOp",EDGE,"E4.right"),sQuery(id+"F14.wireOp",EDGE,"E20.0")])]})});
            var Q1;
            Q1=makeQuery(id+"F15.boolean.opBoolean","COPY",EDGE,{"derivedFrom":makeQuery(id+"F15.opExtrude","SWEPT_EDGE",EDGE,{"disambiguationData":[OSD([sQuery(id+"F0.wireOp",EDGE,"E4.right"),sQuery(id+"F14.wireOp",EDGE,"E21.0")])]})});
            fillet(context, id + "F19", {"entities" : qUnion([Q0, Q1]), "radius" : 5.08 * mm, "tangentPropagation" : true, "allowEdgeOverflow" : false});
        }
        {
            var Q0;
            {var subQ0=sQuery(id+"F0.wireOp",EDGE,"E4.right");var subQ1=makeQuery(id+"F13.opChamfer","BLEND_EDGE",EDGE,{"blendedFrom":[makeQuery(id+"F10.opExtrude","CAP_EDGE",EDGE,{"disambiguationData":[OSD([subQ0])],"isStart":false}),makeQuery(id+"F10.boolean.opBoolean","MERGE",FACE,{"derivedFrom":[makeQuery(id+"F1.opExtrude","SWEPT_FACE",FACE,{"disambiguationData":[OSD([subQ0])]}),makeQuery(id+"F10.opExtrude","SWEPT_FACE",FACE,{"disambiguationData":[OSD([subQ0])]})]})],"blendedInto":[makeQuery(id+"F10.boolean.opBoolean","MERGE",FACE,{"derivedFrom":[makeQuery(id+"F1.opExtrude","SWEPT_FACE",FACE,{"disambiguationData":[OSD([subQ0])]}),makeQuery(id+"F10.opExtrude","SWEPT_FACE",FACE,{"disambiguationData":[OSD([subQ0])]})]})]});Q0=makeQuery(id+"F15.boolean.opBoolean","COPY",FACE,{"derivedFrom":makeQuery(id+"F15.opExtrude","SWEPT_FACE",FACE,{"disambiguationData":[OSD([subQ0]),TDD([makeQuery(id+"F14.imprint","IMPRINT",EDGE,{"disambiguationData":[TD([[makeQuery(id+"F14.imprint","INTERSECT",VERTEX,{"derivedFrom":[subQ1,sQuery(id+"F14.wireOp",EDGE,"E20.0")]}),1.0]])],"derivedFrom":subQ1})])]})});}
            var sketch = newSketch(context, id + "F20", { "sketchPlane" : qUnion([Q0])});
            skCircle(sketch, "E25", {"center": v(156.36, -45.98) * mm, "radius": 19.05 * mm});
            skCircle(sketch, "E26", {"center": v(244.9, -45.98) * mm, "radius": 19.05 * mm});
            skSolve(sketch);
        }
        {
            var Q0;
            Q0=qSketchRegion(id+"F20",true);
            extrude(context, id + "F21", {"entities" : qUnion([Q0]), "operationType" : NewBodyOperationType.REMOVE, "endBound" : BoundingType.THROUGH_ALL, "oppositeDirection" : true, "depth" : 25.4 * mm, "hasSecondDirection" : true, "secondDirectionBound" : SecondDirectionBoundingType.THROUGH_ALL, "secondDirectionOppositeDirection" : false, "secondDirectionDepth" : 25.4 * mm});
        }
    });
